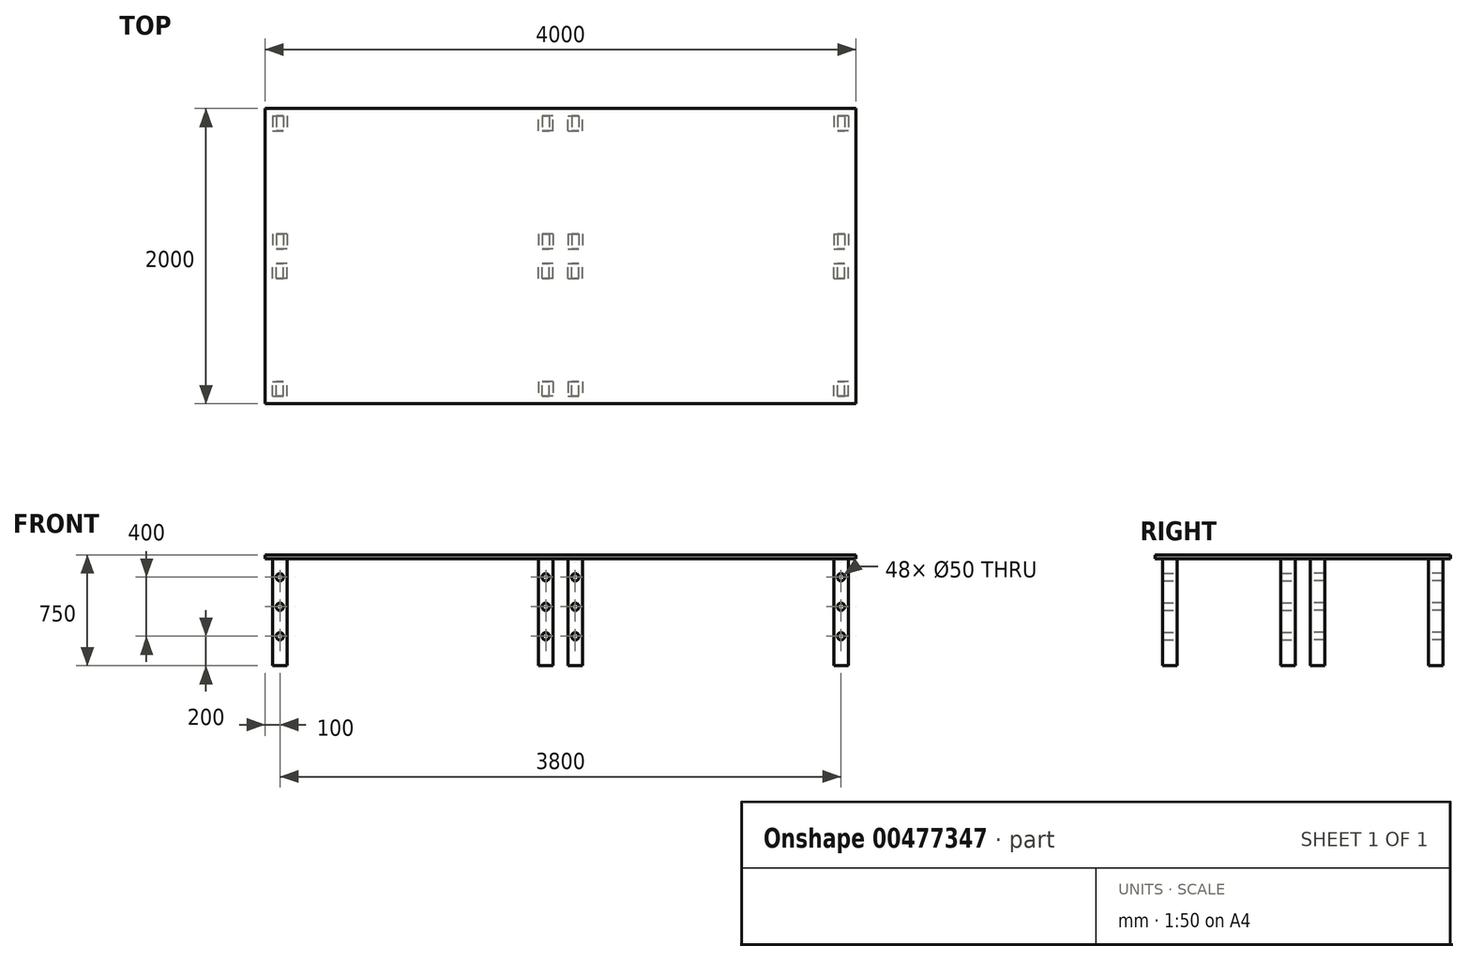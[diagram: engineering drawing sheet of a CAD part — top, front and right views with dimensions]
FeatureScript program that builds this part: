
annotation { "Feature Type Name" : "Feature", "Feature Type Description" : "" }
export const myFeature = defineFeature(function(context is Context, id is Id, definition is map)
    precondition{}
    {
        {
            var Q0;
            Q0=qCreatedBy(makeId("Top.planeOp"),FACE);
            var sketch = newSketch(context, id + "F0", { "sketchPlane" : qUnion([Q0])});
            skLineSegment(sketch, "E0.bottom", {"start": v(0, 0) * mm, "end": v(2000, 0) * mm});
            skLineSegment(sketch, "E0.top", {"start": v(0, 1000) * mm, "end": v(2000, 1000) * mm});
            skLineSegment(sketch, "E0.left", {"start": v(0, 0) * mm, "end": v(0, 1000) * mm});
            skLineSegment(sketch, "E0.right", {"start": v(2000, 0) * mm, "end": v(2000, 1000) * mm});
            skSolve(sketch);
        }
        {
            var Q0;
            Q0=makeQuery(id+"F0.imprint","IMPRINT",FACE,{"disambiguationData":[TD([[makeQuery(id+"F0.imprint","IMPRINT",EDGE,{"derivedFrom":sQuery(id+"F0.wireOp",EDGE,"E0.bottom")}),1.0]])]});
            extrude(context, id + "F1", {"entities" : qUnion([Q0]), "depth" : 25 * mm});
        }
        {
            var Q0;
            Q0=qCreatedBy(makeId("Top.planeOp"),FACE);
            var sketch = newSketch(context, id + "F2", { "sketchPlane" : qUnion([Q0])});
            skLineSegment(sketch, "E1.bottom", {"start": v(50, 150) * mm, "end": v(150, 150) * mm});
            skLineSegment(sketch, "E1.top", {"start": v(50, 50) * mm, "end": v(150, 50) * mm});
            skLineSegment(sketch, "E1.left", {"start": v(50, 150) * mm, "end": v(50, 50) * mm});
            skLineSegment(sketch, "E1.right", {"start": v(150, 150) * mm, "end": v(150, 50) * mm});
            skSolve(sketch);
        }
        {
            var Q0;
            Q0=makeQuery(id+"F2.imprint","IMPRINT",FACE,{"disambiguationData":[TD([[makeQuery(id+"F2.imprint","IMPRINT",EDGE,{"derivedFrom":sQuery(id+"F2.wireOp",EDGE,"E1.bottom")}),-1.0]])]});
            extrude(context, id + "F3", {"entities" : qUnion([Q0]), "operationType" : NewBodyOperationType.ADD, "oppositeDirection" : true, "depth" : 725 * mm});
        }
        {
            var Q0;
            Q0=qCreatedBy(makeId("Top.planeOp"),FACE);
            var sketch = newSketch(context, id + "F4", { "sketchPlane" : qUnion([Q0])});
            skLineSegment(sketch, "E2.bottom", {"start": v(1850, 150) * mm, "end": v(1950, 150) * mm});
            skLineSegment(sketch, "E2.top", {"start": v(1850, 50) * mm, "end": v(1950, 50) * mm});
            skLineSegment(sketch, "E2.left", {"start": v(1850, 150) * mm, "end": v(1850, 50) * mm});
            skLineSegment(sketch, "E2.right", {"start": v(1950, 150) * mm, "end": v(1950, 50) * mm});
            skSolve(sketch);
        }
        {
            var Q0;
            Q0=makeQuery(id+"F4.imprint","IMPRINT",FACE,{"disambiguationData":[TD([[makeQuery(id+"F4.imprint","IMPRINT",EDGE,{"derivedFrom":sQuery(id+"F4.wireOp",EDGE,"E2.bottom")}),-1.0]])]});
            extrude(context, id + "F5", {"entities" : qUnion([Q0]), "operationType" : NewBodyOperationType.ADD, "oppositeDirection" : true, "depth" : 725 * mm});
        }
        {
            var Q0;
            Q0=qCreatedBy(makeId("Top.planeOp"),FACE);
            var sketch = newSketch(context, id + "F6", { "sketchPlane" : qUnion([Q0])});
            skLineSegment(sketch, "E3.bottom", {"start": v(50, 850) * mm, "end": v(150, 850) * mm});
            skLineSegment(sketch, "E3.top", {"start": v(50, 950) * mm, "end": v(150, 950) * mm});
            skLineSegment(sketch, "E3.left", {"start": v(50, 850) * mm, "end": v(50, 950) * mm});
            skLineSegment(sketch, "E3.right", {"start": v(150, 850) * mm, "end": v(150, 950) * mm});
            skSolve(sketch);
        }
        {
            var Q0;
            Q0=makeQuery(id+"F6.imprint","IMPRINT",FACE,{"disambiguationData":[TD([[makeQuery(id+"F6.imprint","IMPRINT",EDGE,{"derivedFrom":sQuery(id+"F6.wireOp",EDGE,"E3.bottom")}),1.0]])]});
            extrude(context, id + "F7", {"entities" : qUnion([Q0]), "operationType" : NewBodyOperationType.ADD, "oppositeDirection" : true, "depth" : 725 * mm});
        }
        {
            var Q0;
            Q0=qCreatedBy(makeId("Top.planeOp"),FACE);
            var sketch = newSketch(context, id + "F8", { "sketchPlane" : qUnion([Q0])});
            skLineSegment(sketch, "E4.bottom", {"start": v(1950, 950) * mm, "end": v(1850, 950) * mm});
            skLineSegment(sketch, "E4.top", {"start": v(1950, 850) * mm, "end": v(1850, 850) * mm});
            skLineSegment(sketch, "E4.left", {"start": v(1950, 950) * mm, "end": v(1950, 850) * mm});
            skLineSegment(sketch, "E4.right", {"start": v(1850, 950) * mm, "end": v(1850, 850) * mm});
            skSolve(sketch);
        }
        {
            var Q0;
            Q0=makeQuery(id+"F8.imprint","IMPRINT",FACE,{"disambiguationData":[TD([[makeQuery(id+"F8.imprint","IMPRINT",EDGE,{"derivedFrom":sQuery(id+"F8.wireOp",EDGE,"E4.bottom")}),1.0]])]});
            extrude(context, id + "F9", {"entities" : qUnion([Q0]), "operationType" : NewBodyOperationType.ADD, "oppositeDirection" : true, "depth" : 725 * mm});
        }
        {
            var Q0;
            Q0=qCreatedBy(makeId("Front.planeOp"),FACE);
            var sketch = newSketch(context, id + "F10", { "sketchPlane" : qUnion([Q0])});
            skCircle(sketch, "E5", {"center": v(100, -525) * mm, "radius": 25 * mm});
            skCircle(sketch, "E6", {"center": v(100, -325) * mm, "radius": 25 * mm});
            skCircle(sketch, "E7", {"center": v(100, -125) * mm, "radius": 25 * mm});
            skSolve(sketch);
        }
        {
            var Q0;
            Q0 = qSketchRegion(id + "F10", true);
            extrude(context, id + "F11", {"entities" : qUnion([Q0]), "operationType" : NewBodyOperationType.REMOVE, "endBound" : BoundingType.THROUGH_ALL, "oppositeDirection" : true, "depth" : 25 * mm});
        }
        {
            var Q0;
            Q0=qCreatedBy(makeId("Front.planeOp"),FACE);
            var sketch = newSketch(context, id + "F12", { "sketchPlane" : qUnion([Q0])});
            skCircle(sketch, "E8", {"center": v(1900, -525) * mm, "radius": 25 * mm});
            skCircle(sketch, "E9", {"center": v(1900, -325) * mm, "radius": 25 * mm});
            skCircle(sketch, "E10", {"center": v(1900, -125) * mm, "radius": 25 * mm});
            skSolve(sketch);
        }
        {
            var Q0;
            Q0 = qSketchRegion(id + "F12", true);
            extrude(context, id + "F13", {"entities" : qUnion([Q0]), "operationType" : NewBodyOperationType.REMOVE, "endBound" : BoundingType.THROUGH_ALL, "oppositeDirection" : true, "depth" : 25 * mm});
        }
        {
            var Q0;
            Q0=makeQuery(id+"F1.opExtrude","SWEPT_BODY",BODY,{"disambiguationData":[OSD([sQuery(id+"F0.wireOp",EDGE,"E0.bottom"),sQuery(id+"F0.wireOp",EDGE,"E0.top"),sQuery(id+"F0.wireOp",EDGE,"E0.left"),sQuery(id+"F0.wireOp",EDGE,"E0.right")])]});
            var Q1;
            Q1=qCreatedBy(makeId("Right.planeOp"),FACE);
            mirror(context, id + "F15", {"operationType" : NewBodyOperationType.ADD, "entities" : qUnion([Q0]), "mirrorPlane" : qUnion([Q1])});
        }
        {
            var Q0;
            Q0=makeQuery(id+"F1.opExtrude","SWEPT_BODY",BODY,{"disambiguationData":[OSD([sQuery(id+"F0.wireOp",EDGE,"E0.bottom"),sQuery(id+"F0.wireOp",EDGE,"E0.top"),sQuery(id+"F0.wireOp",EDGE,"E0.left"),sQuery(id+"F0.wireOp",EDGE,"E0.right")])]});
            var Q1;
            Q1=qCreatedBy(makeId("Front.planeOp"),FACE);
            mirror(context, id + "F16", {"operationType" : NewBodyOperationType.ADD, "entities" : qUnion([Q0]), "mirrorPlane" : qUnion([Q1])});
        }
    });
